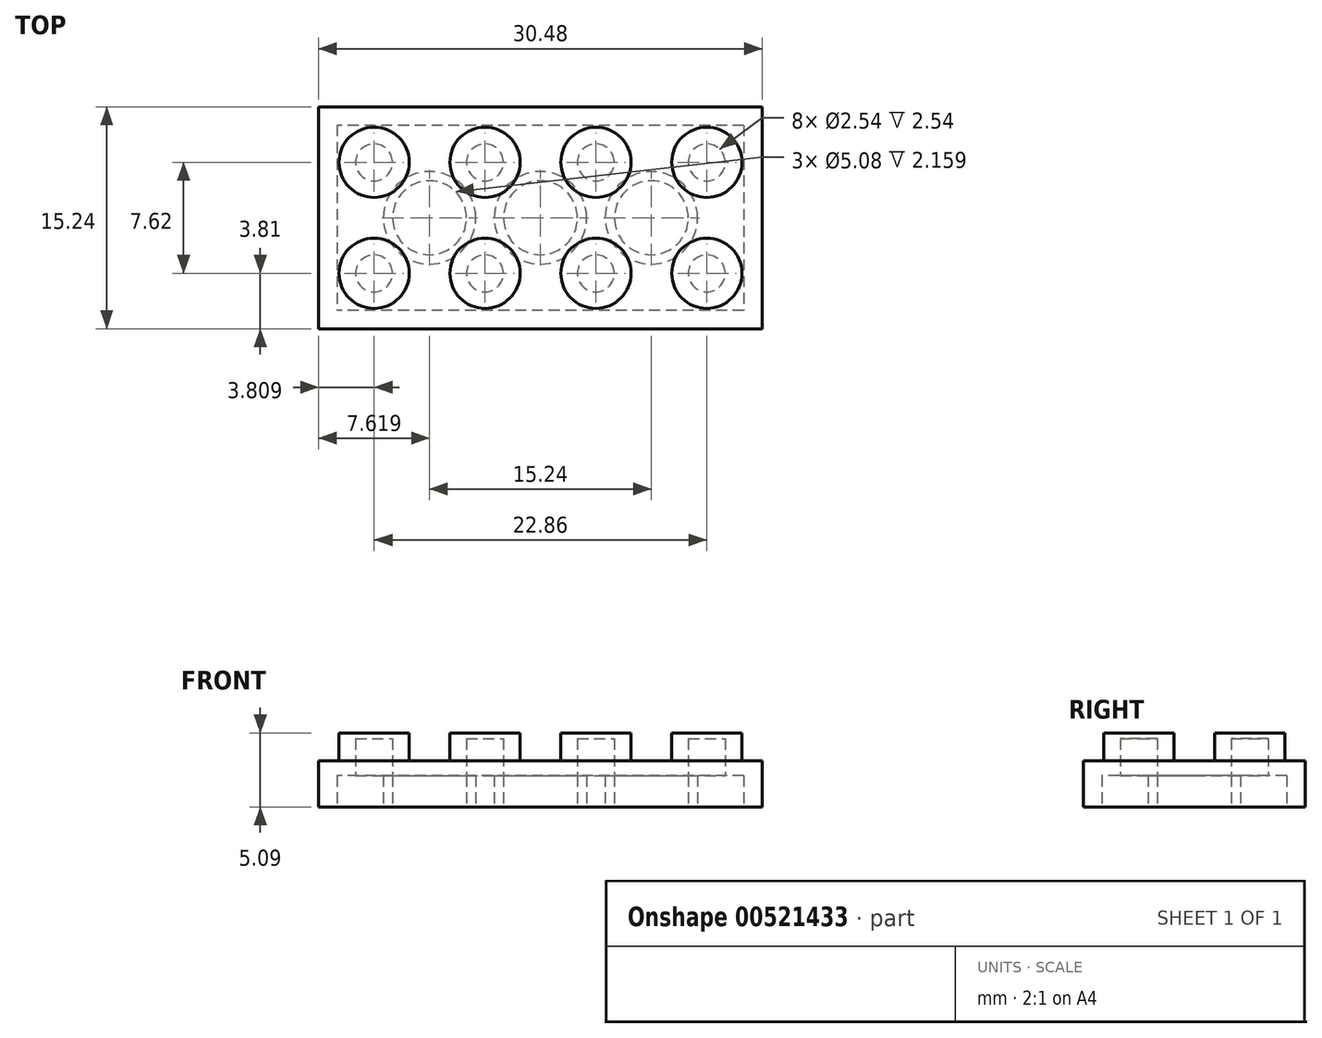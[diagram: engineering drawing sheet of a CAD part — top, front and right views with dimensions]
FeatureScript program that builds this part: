
annotation { "Feature Type Name" : "Feature", "Feature Type Description" : "" }
export const myFeature = defineFeature(function(context is Context, id is Id, definition is map)
    precondition{}
    {
        {
            var Q0;
            Q0=qCreatedBy(makeId("Top.planeOp"),FACE);
            var sketch = newSketch(context, id + "F0", { "sketchPlane" : qUnion([Q0])});
            skLineSegment(sketch, "E0.bottom", {"start": v(-53.47, 28.84) * mm, "end": v(-23, 28.84) * mm});
            skLineSegment(sketch, "E0.top", {"start": v(-53.47, 13.6) * mm, "end": v(-23, 13.6) * mm});
            skLineSegment(sketch, "E0.left", {"start": v(-53.47, 28.84) * mm, "end": v(-53.47, 13.6) * mm});
            skLineSegment(sketch, "E0.right", {"start": v(-23, 28.84) * mm, "end": v(-23, 13.6) * mm});
            skSolve(sketch);
        }
        {
            var Q0;
            Q0=makeQuery(id+"F0.imprint","IMPRINT",FACE,{"disambiguationData":[TD([[makeQuery(id+"F0.imprint","IMPRINT",EDGE,{"derivedFrom":sQuery(id+"F0.wireOp",EDGE,"E0.bottom")}),-1.0]])]});
            var sketch = newSketch(context, id + "F1", { "sketchPlane" : qUnion([Q0])});
            skCircle(sketch, "E1", {"center": v(-26.8, 25.03) * mm, "radius": 2.41 * mm});
            skCircle(sketch, "E2", {"center": v(-26.8, 17.41) * mm, "radius": 2.41 * mm});
            skCircle(sketch, "E3", {"center": v(-34.42, 25.03) * mm, "radius": 2.41 * mm});
            skCircle(sketch, "E4", {"center": v(-34.42, 17.41) * mm, "radius": 2.41 * mm});
            skCircle(sketch, "E5", {"center": v(-42.04, 25.03) * mm, "radius": 2.41 * mm});
            skCircle(sketch, "E6", {"center": v(-42.04, 17.41) * mm, "radius": 2.41 * mm});
            skCircle(sketch, "E7", {"center": v(-49.66, 25.03) * mm, "radius": 2.41 * mm});
            skCircle(sketch, "E8", {"center": v(-49.66, 17.41) * mm, "radius": 2.41 * mm});
            skSolve(sketch);
        }
        {
            var Q0;
            Q0=qSketchRegion(id+"F0",true);
            extrude(context, id + "F2", {"entities" : qUnion([Q0]), "oppositeDirection" : true, "depth" : 3.17 * mm});
        }
        {
            var Q0;
            Q0=qSketchRegion(id+"F1",true);
            extrude(context, id + "F3", {"entities" : qUnion([Q0]), "operationType" : NewBodyOperationType.ADD, "depth" : 1.9 * mm});
        }
        {
            var Q0;
            Q0=makeQuery(id+"F2.opExtrude","CAP_FACE",FACE,{"disambiguationData":[OSD([sQuery(id+"F0.wireOp",EDGE,"E0.bottom"),sQuery(id+"F0.wireOp",EDGE,"E0.top"),sQuery(id+"F0.wireOp",EDGE,"E0.left"),sQuery(id+"F0.wireOp",EDGE,"E0.right")])],"isStart":false});
            var sketch = newSketch(context, id + "F4", { "sketchPlane" : qUnion([Q0])});
            skCircle(sketch, "E9", {"center": v(-30.61, -21.22) * mm, "radius": 2.54 * mm});
            skCircle(sketch, "E10", {"center": v(-30.61, -21.22) * mm, "radius": 3.18 * mm});
            skCircle(sketch, "E11", {"center": v(-38.23, -21.22) * mm, "radius": 2.54 * mm});
            skPoint(sketch, "E11.centerSnap0", {"position": v(-38.23, -13.6) * mm});
            skCircle(sketch, "E12", {"center": v(-38.23, -21.22) * mm, "radius": 3.18 * mm});
            skCircle(sketch, "E13", {"center": v(-45.85, -21.22) * mm, "radius": 2.54 * mm});
            skCircle(sketch, "E14", {"center": v(-45.85, -21.22) * mm, "radius": 3.18 * mm});
            skLineSegment(sketch, "E15.bottom", {"start": v(-24.26, -27.57) * mm, "end": v(-52.2, -27.57) * mm});
            skLineSegment(sketch, "E15.top", {"start": v(-24.26, -14.87) * mm, "end": v(-52.2, -14.87) * mm});
            skLineSegment(sketch, "E15.left", {"start": v(-24.26, -27.57) * mm, "end": v(-24.26, -14.87) * mm});
            skLineSegment(sketch, "E15.right", {"start": v(-52.2, -27.57) * mm, "end": v(-52.2, -14.87) * mm});
            skSolve(sketch);
        }
        {
            var Q0;
            Q0=makeQuery(id+"F4.imprint","IMPRINT",FACE,{"disambiguationData":[TD([[makeQuery(id+"F4.imprint","IMPRINT",EDGE,{"derivedFrom":sQuery(id+"F4.wireOp",EDGE,"E15.bottom")}),1.0]])]});
            var sketch = newSketch(context, id + "F5", { "sketchPlane" : qUnion([Q0])});
            skCircle(sketch, "E16", {"center": v(-26.8, -25.03) * mm, "radius": 1.27 * mm});
            skCircle(sketch, "E17", {"center": v(-34.42, -25.03) * mm, "radius": 1.27 * mm});
            skCircle(sketch, "E18", {"center": v(-42.04, -25.03) * mm, "radius": 1.27 * mm});
            skCircle(sketch, "E19", {"center": v(-49.66, -25.03) * mm, "radius": 1.27 * mm});
            skCircle(sketch, "E20", {"center": v(-26.8, -17.41) * mm, "radius": 1.27 * mm});
            skCircle(sketch, "E21", {"center": v(-34.42, -17.41) * mm, "radius": 1.27 * mm});
            skCircle(sketch, "E22", {"center": v(-42.04, -17.41) * mm, "radius": 1.27 * mm});
            skCircle(sketch, "E23", {"center": v(-49.66, -17.41) * mm, "radius": 1.27 * mm});
            skSolve(sketch);
        }
        {
            var Q0;
            Q0=qSketchRegion(id+"F5",true);
            extrude(context, id + "F6", {"entities" : qUnion([Q0]), "operationType" : NewBodyOperationType.REMOVE, "oppositeDirection" : true, "depth" : 4.7 * mm});
        }
        {
            var Q0;
            Q0=qSketchRegion(id+"F4",true);
            extrude(context, id + "F7", {"entities" : qUnion([Q0]), "operationType" : NewBodyOperationType.REMOVE, "oppositeDirection" : true, "depth" : 2.16 * mm});
        }
        {
            var Q0;
            Q0=makeQuery(id+"F5.imprint","IMPRINT",FACE,{"disambiguationData":[TD([[makeQuery(id+"F5.imprint","IMPRINT",EDGE,{"derivedFrom":sQuery(id+"F5.wireOp",EDGE,"E19")}),1.0]])]});
            extrude(context, id + "F8", {"entities" : qUnion([Q0]), "operationType" : NewBodyOperationType.ADD, "oppositeDirection" : true, "depth" : 4.7 * mm});
        }
        {
            var Q0;
            Q0=makeQuery(id+"F5.imprint","IMPRINT",FACE,{"disambiguationData":[TD([[makeQuery(id+"F5.imprint","IMPRINT",EDGE,{"derivedFrom":sQuery(id+"F5.wireOp",EDGE,"E19")}),1.0]])]});
            extrude(context, id + "F9", {"entities" : qUnion([Q0]), "operationType" : NewBodyOperationType.REMOVE, "oppositeDirection" : true, "depth" : 4.7 * mm});
        }
        {
            var Q0;
            Q0=makeQuery(id+"F4.imprint","IMPRINT",FACE,{"disambiguationData":[TD([[makeQuery(id+"F4.imprint","IMPRINT",EDGE,{"derivedFrom":sQuery(id+"F4.wireOp",EDGE,"E13")}),1.0]])]});
            var Q1;
            Q1=sQuery(id+"F4.wireOp",EDGE,"E13");
            var Q2;
            Q2=sQuery(id+"F4.wireOp",EDGE,"E11");
            var Q3;
            Q3=sQuery(id+"F4.wireOp",EDGE,"E9");
            extrude(context, id + "F10", {"entities" : qUnion([Q0]), "operationType" : NewBodyOperationType.REMOVE, "surfaceEntities" : qUnion([Q1, Q2, Q3]), "oppositeDirection" : true, "depth" : 2.16 * mm});
        }
        {
            var Q0;
            Q0=makeQuery(id+"F4.imprint","IMPRINT",FACE,{"disambiguationData":[TD([[makeQuery(id+"F4.imprint","IMPRINT",EDGE,{"derivedFrom":sQuery(id+"F4.wireOp",EDGE,"E9")}),1.0]])]});
            extrude(context, id + "F11", {"entities" : qUnion([Q0]), "operationType" : NewBodyOperationType.REMOVE, "oppositeDirection" : true, "depth" : 2.16 * mm});
        }
        {
            var Q0;
            Q0=makeQuery(id+"F4.imprint","IMPRINT",FACE,{"disambiguationData":[TD([[makeQuery(id+"F4.imprint","IMPRINT",EDGE,{"derivedFrom":sQuery(id+"F4.wireOp",EDGE,"E11")}),1.0]])]});
            extrude(context, id + "F12", {"entities" : qUnion([Q0]), "operationType" : NewBodyOperationType.REMOVE, "oppositeDirection" : true, "depth" : 2.16 * mm});
        }
    });
